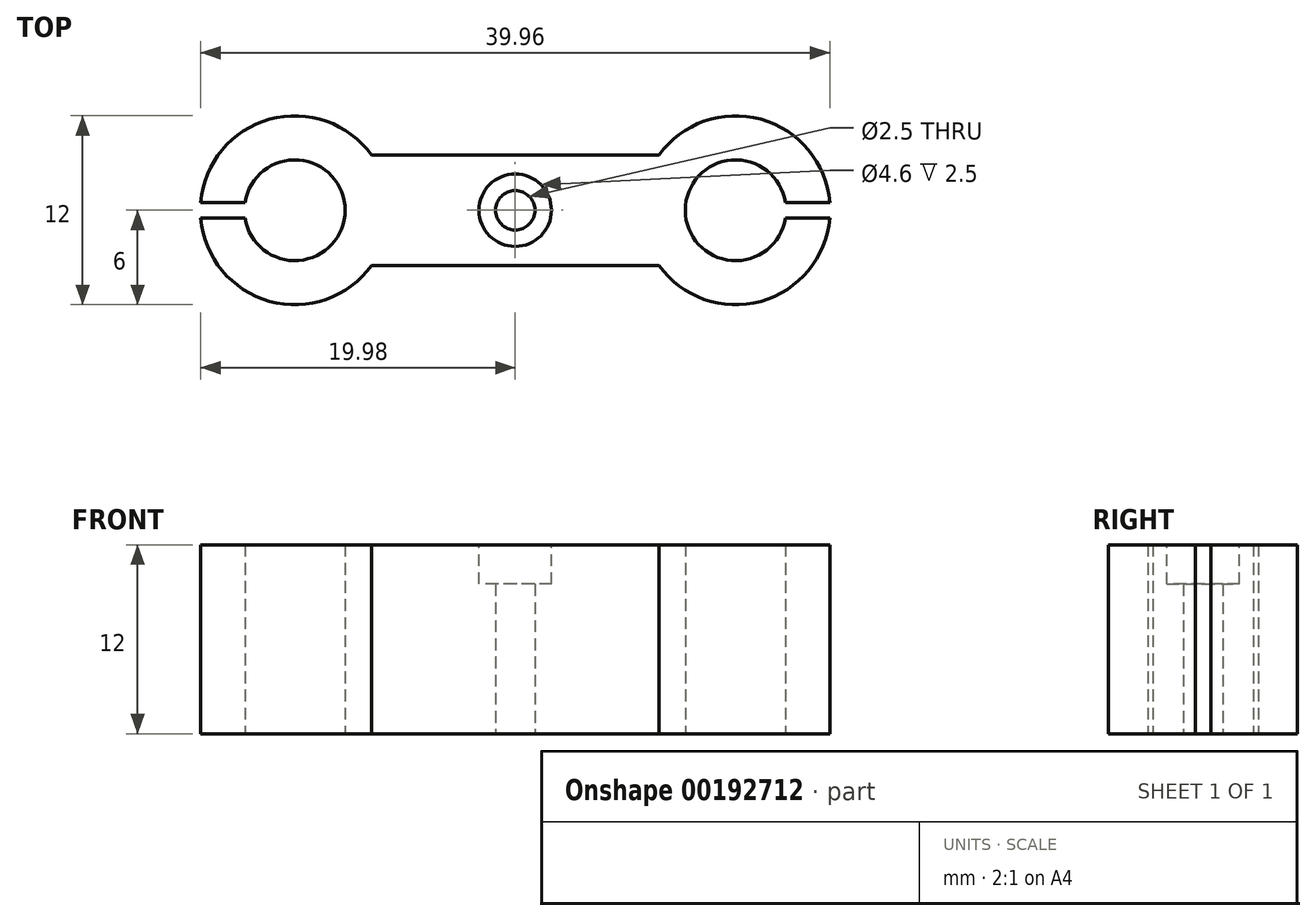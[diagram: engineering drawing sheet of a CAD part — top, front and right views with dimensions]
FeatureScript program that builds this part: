
annotation { "Feature Type Name" : "Feature", "Feature Type Description" : "" }
export const myFeature = defineFeature(function(context is Context, id is Id, definition is map)
    precondition{}
    {
        {
            var Q0;
            Q0=qCreatedBy(makeId("Top.planeOp"),FACE);
            var sketch = newSketch(context, id + "F0", { "sketchPlane" : qUnion([Q0])});
            skArc(sketch, "E0", {"start": v(-9.13, 3.5) * mm, "mid": v(-15.6, 5.78) * mm, "end": v(-19.98, 0.5) * mm});
            skArc(sketch, "E1", {"start": v(9.13, -3.5) * mm, "mid": v(15.6, -5.78) * mm, "end": v(19.98, -0.5) * mm});
            skLineSegment(sketch, "E2", {"start": v(-9.13, 3.5) * mm, "end": v(9.13, 3.5) * mm});
            skLineSegment(sketch, "E3", {"start": v(-9.13, -3.5) * mm, "end": v(9.13, -3.5) * mm});
            skArc(sketch, "E4", {"start": v(-17.16, -0.5) * mm, "mid": v(-10.8, 0) * mm, "end": v(-17.16, 0.5) * mm});
            skArc(sketch, "E5", {"start": v(17.16, 0.5) * mm, "mid": v(10.8, 0) * mm, "end": v(17.16, -0.5) * mm});
            skLineSegment(sketch, "E6.bottom", {"start": v(-19.98, 0.5) * mm, "end": v(-17.16, 0.5) * mm});
            skLineSegment(sketch, "E6.top", {"start": v(-19.98, -0.5) * mm, "end": v(-17.16, -0.5) * mm});
            skLineSegment(sketch, "E7.bottom", {"start": v(17.16, 0.5) * mm, "end": v(19.98, 0.5) * mm});
            skLineSegment(sketch, "E7.top", {"start": v(17.16, -0.5) * mm, "end": v(19.98, -0.5) * mm});
            skPoint(sketch, "E8.orphan", {"position": v(-21.73, 0.5) * mm});
            skPoint(sketch, "E9.orphan", {"position": v(-21.73, -0.5) * mm});
            skArc(sketch, "E10.trimOffspring", {"start": v(-19.98, -0.5) * mm, "mid": v(-15.6, -5.78) * mm, "end": v(-9.13, -3.5) * mm});
            skArc(sketch, "E11.trimOffspring", {"start": v(19.98, 0.5) * mm, "mid": v(15.6, 5.78) * mm, "end": v(9.13, 3.5) * mm});
            skPoint(sketch, "E7.right.end.orphan", {"position": v(21.78, -0.5) * mm});
            skPoint(sketch, "E7.right.start.orphan", {"position": v(21.78, 0.5) * mm});
            skCircle(sketch, "E12", {"center": v(0, 0) * mm, "radius": 1.25 * mm});
            skSolve(sketch);
        }
        {
            var Q0;
            Q0 = qSketchRegion(id + "F0", true);
            extrude(context, id + "F1", {"entities" : qUnion([Q0]), "depth" : 12 * mm});
        }
        {
            var Q0;
            Q0=makeQuery(id+"F1.opExtrude","CAP_FACE",FACE,{"disambiguationData":[OSD([sQuery(id+"F0.wireOp",EDGE,"E0"),sQuery(id+"F0.wireOp",EDGE,"E1"),sQuery(id+"F0.wireOp",EDGE,"E2"),sQuery(id+"F0.wireOp",EDGE,"E3"),sQuery(id+"F0.wireOp",EDGE,"E4"),sQuery(id+"F0.wireOp",EDGE,"E5"),sQuery(id+"F0.wireOp",EDGE,"E6.bottom"),sQuery(id+"F0.wireOp",EDGE,"E6.top"),sQuery(id+"F0.wireOp",EDGE,"E7.bottom"),sQuery(id+"F0.wireOp",EDGE,"E7.top"),sQuery(id+"F0.wireOp",EDGE,"E10.trimOffspring"),sQuery(id+"F0.wireOp",EDGE,"E11.trimOffspring"),sQuery(id+"F0.wireOp",EDGE,"E12")])],"isStart":false});
            var sketch = newSketch(context, id + "F2", { "sketchPlane" : qUnion([Q0])});
            skCircle(sketch, "E13", {"center": v(0, 0) * mm, "radius": 2.3 * mm});
            skSolve(sketch);
        }
        {
            var Q0;
            Q0 = qSketchRegion(id + "F2", true);
            extrude(context, id + "F3", {"entities" : qUnion([Q0]), "operationType" : NewBodyOperationType.REMOVE, "oppositeDirection" : true, "depth" : 2.5 * mm});
        }
    });
